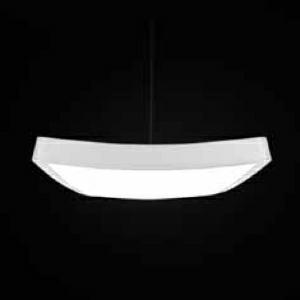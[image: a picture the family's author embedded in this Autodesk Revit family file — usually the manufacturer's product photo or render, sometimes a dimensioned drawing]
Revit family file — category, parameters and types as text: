
# Revit family: spectral_jep_jep-pe-led_5000-840_w
name_source: partatom
category: Lighting Fixtures
revit_build: Autodesk Revit 2016 (Build: 20150220_1215(x64)
units: mm (PartAtom-declared; Revit-internal decimal feet)

## family parameters
Cut with Voids When Loaded = No
Host = Face
Light Source = No
Part Type = Normal
Room Calculation Point = No
Round Connector Dimension = Use Diameter
Shared = No

## types (1)
- SPECTRAL JEP (1 x )
    Apparent Load = 0 VA
    Approval mark = CE
    CIE Flux Codes = 62 88 97 68 100
    Control Gear = Electronic transformer
    Default Elevation = 1800 mm
    Description = SPJ0000005
LED pendant luminaire JEP

Design:
Luminaire housing made of painted plastic with high-efficiency curved mircroprism panel in transparent acrylic. Embossed powder-coated steel gear tray to accommodate and cool the LED cluster. Suspended by means of a transparent power supply cable from an attractive external ceiling canopy. Canopy features a toolless opening plastic cover for convenient ceiling mounting and accommodates the electronic gear for the LEDs. The microprism diffuser panel ensures extremely homogenous light distribution without multiple shadows. Light output ratio equivalent to 2x T16 54W lamps. Closed to the top, predominantly direct light distribution. Indirect LED strips to brighten the ceiling and for room modulation. Basic pendant length setting adjustable with the steel wire at the luminaire, cable adjustable at the ceiling canopy. Junction box in hot-dip galvanised steel with plastic cover. Protection rating IP20, safety class I.

Colour:
Gear tray – similar to RAL 9016 white silk matt
Housing – 3 optional colours, spectral finish
Canopy – similar to RAL 9016 white silk matt
    Height = 35 mm
    Lamp = 1 x
    Lamp count = 1
    Length = 935 mm
    Luminous efficacy = 0 lm/W
    Manufacturer = Ridi
    ModVariant = No
    Model = JEP-PE-LED 5000-840 W
    Mounting Place = Ceiling
    Mounting Type = Pendant
    Number of Poles = 1
    OnlyDefault = Yes
    Power Factor = 1
    Product Name = SPECTRAL JEP
    Product group = Pendant luminaire
    ProductGroupID = 9
    Protection Class = Protection class
    Protection Degree = IP 20
    RlxData = <blob elided: 28713 chars, md5=f5d490f1>
    Socket = socket
    Standby Power = 0 W
    System Light Flux = 0 lm
    System Power = 0 W
    Type Image = jep_pendel.jpg
    URL = http://reluxnet.relux.com
    VarID = 1
    Voltage = 0 V
    Weight = 0.00 kg
    Width = 360 mm

## geometry (parser evidence)
native form markers: Blend x4, Sweep x13
no freeform markers — native parametric forms only
